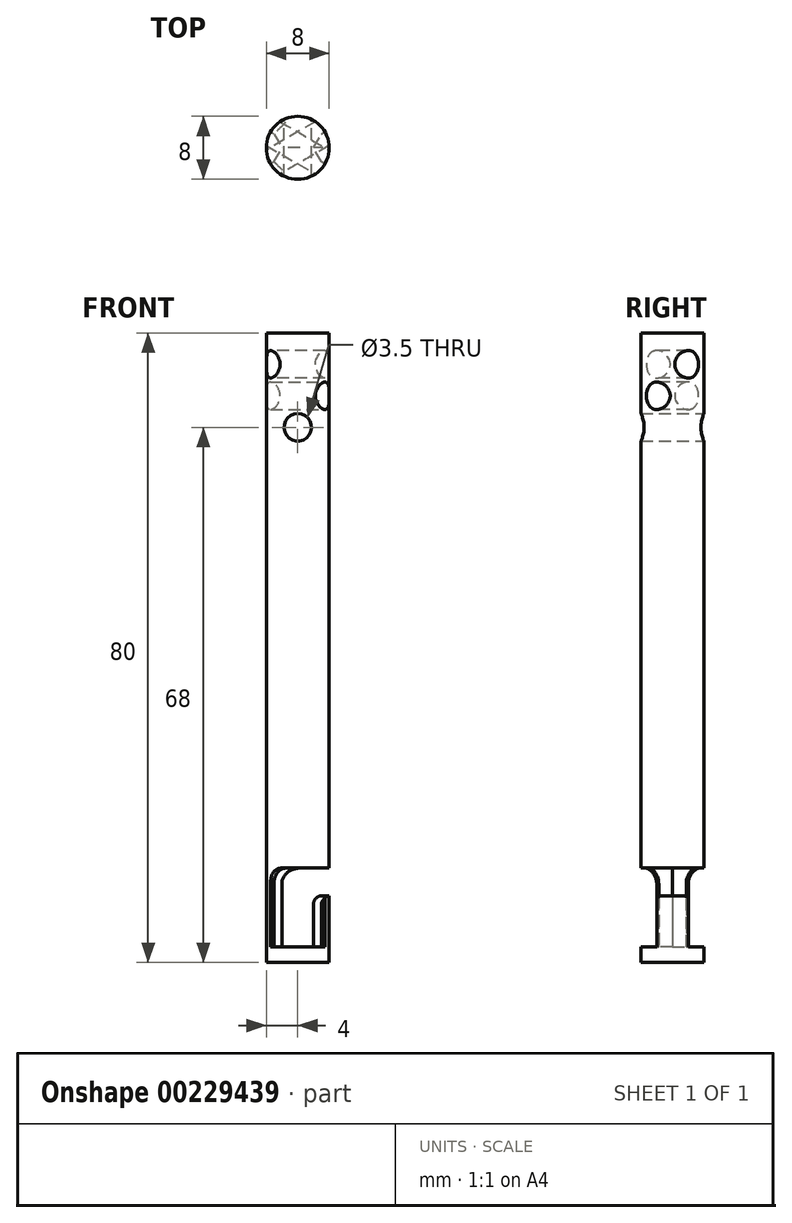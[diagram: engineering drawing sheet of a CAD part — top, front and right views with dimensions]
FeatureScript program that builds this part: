
annotation { "Feature Type Name" : "Feature", "Feature Type Description" : "" }
export const myFeature = defineFeature(function(context is Context, id is Id, definition is map)
    precondition{}
    {
        {
            var Q0;
            Q0=qCreatedBy(makeId("Top.planeOp"),FACE);
            cPlane(context, id + "F0", {"entities" : qUnion([Q0]), "cplaneType" : CPlaneType.OFFSET, "offset" : 1 * mm, "width" : 150 * mm, "height" : 150 * mm});
        }
        {
            var Q0;
            Q0=qCreatedBy(makeId("Front.planeOp"),FACE);
            var sketch = newSketch(context, id + "F1", { "sketchPlane" : qUnion([Q0])});
            skLineSegment(sketch, "E0", {"start": v(0, 0) * mm, "end": v(0, 56.56) * mm});
            skSolve(sketch);
        }
        {
            var Q0;
            Q0=sQuery(id+"F1.wireOp",EDGE,"E0");
            var Q1;
            Q1=qCreatedBy(makeId("Front.planeOp"),FACE);
            cPlane(context, id + "F2", {"entities" : qUnion([Q0, Q1]), "cplaneType" : CPlaneType.LINE_ANGLE, "offset" : 25 * mm, "angle" : 60 * degree, "width" : 150 * mm, "height" : 150 * mm});
        }
        {
            var Q0;
            Q0=sQuery(id+"F1.wireOp",EDGE,"E0");
            var Q1;
            Q1=qCreatedBy(makeId("Front.planeOp"),FACE);
            cPlane(context, id + "F3", {"entities" : qUnion([Q0, Q1]), "cplaneType" : CPlaneType.LINE_ANGLE, "offset" : 25 * mm, "angle" : 120 * degree, "width" : 150 * mm, "height" : 150 * mm});
        }
        {
            var Q0;
            Q0=qCreatedBy(makeId("Front.planeOp"),FACE);
            var sketch = newSketch(context, id + "F4", { "sketchPlane" : qUnion([Q0])});
            skCircle(sketch, "E1", {"center": v(0, 8) * mm, "radius": 1.75 * mm});
            skSolve(sketch);
        }
        {
            var Q0;
            Q0=qCreatedBy(id+"F2.planeOp",FACE);
            var sketch = newSketch(context, id + "F5", { "sketchPlane" : qUnion([Q0])});
            skCircle(sketch, "E2", {"center": v(0, 12) * mm, "radius": 1.75 * mm});
            skSolve(sketch);
        }
        {
            var Q0;
            Q0=qCreatedBy(id+"F3.planeOp",FACE);
            var sketch = newSketch(context, id + "F6", { "sketchPlane" : qUnion([Q0])});
            skCircle(sketch, "E3", {"center": v(0, 16) * mm, "radius": 1.75 * mm});
            skSolve(sketch);
        }
        {
            var Q0;
            Q0=qCreatedBy(id+"F0.planeOp",FACE);
            var sketch = newSketch(context, id + "F7", { "sketchPlane" : qUnion([Q0])});
            skCircle(sketch, "E4", {"center": v(0, 0) * mm, "radius": 4 * mm});
            skSolve(sketch);
        }
        {
            var Q0;
            Q0=makeQuery(id+"F7.imprint","IMPRINT",FACE,{"disambiguationData":[TD([[makeQuery(id+"F7.imprint","IMPRINT",EDGE,{"derivedFrom":sQuery(id+"F7.wireOp",EDGE,"E4")}),1.0]])]});
            extrude(context, id + "F8", {"entities" : qUnion([Q0]), "depth" : 19 * mm, "hasSecondDirection" : true, "secondDirectionOppositeDirection" : true, "secondDirectionDepth" : 61 * mm});
        }
        {
            var Q0;
            Q0 = qSketchRegion(id + "F6", true);
            extrude(context, id + "F9", {"entities" : qUnion([Q0]), "operationType" : NewBodyOperationType.REMOVE, "endBound" : BoundingType.UP_TO_NEXT, "oppositeDirection" : true, "depth" : 25 * mm, "hasSecondDirection" : true, "secondDirectionOppositeDirection" : false, "secondDirectionDepth" : 25 * mm});
        }
        {
            var Q0;
            Q0 = qSketchRegion(id + "F5", true);
            extrude(context, id + "F10", {"entities" : qUnion([Q0]), "operationType" : NewBodyOperationType.REMOVE, "endBound" : BoundingType.UP_TO_NEXT, "depth" : 25 * mm, "hasSecondDirection" : true, "secondDirectionBound" : SecondDirectionBoundingType.UP_TO_NEXT, "secondDirectionOppositeDirection" : true, "secondDirectionDepth" : 25 * mm});
        }
        {
            var Q0;
            Q0 = qSketchRegion(id + "F4", true);
            extrude(context, id + "F11", {"entities" : qUnion([Q0]), "operationType" : NewBodyOperationType.REMOVE, "endBound" : BoundingType.UP_TO_NEXT, "depth" : 25 * mm, "hasSecondDirection" : true, "secondDirectionBound" : SecondDirectionBoundingType.UP_TO_NEXT, "secondDirectionOppositeDirection" : true, "secondDirectionDepth" : 25 * mm});
        }
        {
            var Q0;
            Q0=qCreatedBy(makeId("Front.planeOp"),FACE);
            var sketch = newSketch(context, id + "F12", { "sketchPlane" : qUnion([Q0])});
            skLineSegment(sketch, "E5.bottom", {"start": v(-1.75, -58) * mm, "end": v(1.75, -58) * mm});
            skLineSegment(sketch, "E5.top", {"start": v(-1.75, -48) * mm, "end": v(1.75, -48) * mm});
            skLineSegment(sketch, "E5.left", {"start": v(-1.75, -58) * mm, "end": v(-1.75, -48) * mm});
            skLineSegment(sketch, "E5.right", {"start": v(1.75, -58) * mm, "end": v(1.75, -48) * mm});
            skLineSegment(sketch, "E6.bottom", {"start": v(-1.75, -48) * mm, "end": v(6.64, -48) * mm});
            skLineSegment(sketch, "E6.top", {"start": v(-1.75, -51.5) * mm, "end": v(6.64, -51.5) * mm});
            skLineSegment(sketch, "E6.left", {"start": v(-1.75, -48) * mm, "end": v(-1.75, -51.5) * mm});
            skLineSegment(sketch, "E6.right", {"start": v(6.64, -48) * mm, "end": v(6.64, -51.5) * mm});
            skSolve(sketch);
        }
        {
            var Q0;
            Q0=qCreatedBy(makeId("Right.planeOp"),FACE);
            var sketch = newSketch(context, id + "F13", { "sketchPlane" : qUnion([Q0])});
            skLineSegment(sketch, "E7.bottom", {"start": v(-7, -58) * mm, "end": v(-1, -58) * mm});
            skLineSegment(sketch, "E7.top", {"start": v(-7, -48) * mm, "end": v(-1, -48) * mm});
            skLineSegment(sketch, "E7.left", {"start": v(-7, -58) * mm, "end": v(-7, -48) * mm});
            skLineSegment(sketch, "E7.right", {"start": v(-1, -58) * mm, "end": v(-1, -48) * mm});
            skSolve(sketch);
        }
        {
            var Q0;
            Q0=makeQuery(id+"F13.imprint","IMPRINT",FACE,{"disambiguationData":[TD([[makeQuery(id+"F13.imprint","IMPRINT",EDGE,{"derivedFrom":sQuery(id+"F13.wireOp",EDGE,"E7.bottom")}),1.0]])]});
            var Q1;
            Q1=sQuery(id+"F13.wireOp",EDGE,"E7.left");
            var Q2;
            Q2=sQuery(id+"F1.wireOp",EDGE,"E0");
            revolve(context, id + "F14", {"operationType" : NewBodyOperationType.REMOVE, "surfaceOperationType" : NewSurfaceOperationType.NEW, "entities" : qUnion([Q0]), "surfaceEntities" : qUnion([Q1]), "axis" : qUnion([Q2]), "revolveType" : RevolveType.SYMMETRIC, "oppositeDirection" : true, "angle" : 120 * degree});
        }
        {
            var Q0;
            Q0=qCreatedBy(makeId("Right.planeOp"),FACE);
            var sketch = newSketch(context, id + "F15", { "sketchPlane" : qUnion([Q0])});
            skLineSegment(sketch, "E8.bottom", {"start": v(1, -58) * mm, "end": v(7, -58) * mm});
            skLineSegment(sketch, "E8.top", {"start": v(1, -48) * mm, "end": v(7, -48) * mm});
            skLineSegment(sketch, "E8.left", {"start": v(1, -58) * mm, "end": v(1, -48) * mm});
            skLineSegment(sketch, "E8.right", {"start": v(7, -58) * mm, "end": v(7, -48) * mm});
            skSolve(sketch);
        }
        {
            var Q0;
            Q0 = qSketchRegion(id + "F15", true);
            var Q1;
            Q1=sQuery(id+"F1.wireOp",EDGE,"E0");
            revolve(context, id + "F16", {"operationType" : NewBodyOperationType.REMOVE, "surfaceOperationType" : NewSurfaceOperationType.NEW, "entities" : qUnion([Q0]), "axis" : qUnion([Q1]), "revolveType" : RevolveType.SYMMETRIC, "angle" : 120 * degree});
        }
        {
            var Q0;
            Q0 = qSketchRegion(id + "F12", true);
            var Q1;
            Q1=sQuery(id+"F12.wireOp",EDGE,"SAmgIPEb-TWhO-SjVr-rJ2Y-Q6ch8T96Yinj");
            var Q2;
            Q2=sQuery(id+"F12.wireOp",EDGE,"V83VEsyv-MSzQ-oQPX-2e80-Iq0brfELiZnj.bottom");
            var Q3;
            Q3=sQuery(id+"F12.wireOp",EDGE,"V83VEsyv-MSzQ-oQPX-2e80-Iq0brfELiZnj.right");
            var Q4;
            Q4=sQuery(id+"F12.wireOp",EDGE,"V83VEsyv-MSzQ-oQPX-2e80-Iq0brfELiZnj.top");
            var Q5;
            Q5=sQuery(id+"F12.wireOp",EDGE,"7jSH2nb5-ehXd-Dpum-2Iuk-bTiolaQdSqVP.left");
            var Q6;
            Q6=sQuery(id+"F12.wireOp",EDGE,"7jSH2nb5-ehXd-Dpum-2Iuk-bTiolaQdSqVP.right");
            var Q7;
            Q7=sQuery(id+"F12.wireOp",EDGE,"cEcL3S88-yEdN-HCXQ-9xUG-hMFvsOIPaXgE");
            extrude(context, id + "F17", {"entities" : qUnion([Q0]), "operationType" : NewBodyOperationType.REMOVE, "surfaceEntities" : qUnion([Q1, Q2, Q3, Q4, Q5, Q6, Q7]), "oppositeDirection" : true, "depth" : 25 * mm, "hasSecondDirection" : true, "secondDirectionOppositeDirection" : false, "secondDirectionDepth" : 25 * mm});
        }
        {
            var Q0;
            Q0=qCreatedBy(makeId("Front.planeOp"),FACE);
            var Q1;
            Q1=sQuery(id+"F1.wireOp",EDGE,"E0");
            cPlane(context, id + "F18", {"entities" : qUnion([Q0, Q1]), "cplaneType" : CPlaneType.LINE_ANGLE, "offset" : 25 * mm, "angle" : 30 * degree, "width" : 150 * mm, "height" : 150 * mm});
        }
        {
            var Q0;
            Q0=qCreatedBy(makeId("Front.planeOp"),FACE);
            var Q1;
            Q1=sQuery(id+"F1.wireOp",EDGE,"E0");
            cPlane(context, id + "F19", {"entities" : qUnion([Q0, Q1]), "cplaneType" : CPlaneType.LINE_ANGLE, "offset" : 25 * mm, "angle" : -30 * degree, "width" : 150 * mm, "height" : 150 * mm});
        }
        {
            var Q0;
            Q0=qCreatedBy(id+"F18.planeOp",FACE);
            var sketch = newSketch(context, id + "F20", { "sketchPlane" : qUnion([Q0])});
            skLineSegment(sketch, "E9.bottom", {"start": v(1.75, -48) * mm, "end": v(-1.75, -48) * mm});
            skLineSegment(sketch, "E9.top", {"start": v(1.75, -58) * mm, "end": v(-1.75, -58) * mm});
            skLineSegment(sketch, "E9.left", {"start": v(1.75, -48) * mm, "end": v(1.75, -58) * mm});
            skLineSegment(sketch, "E9.right", {"start": v(-1.75, -48) * mm, "end": v(-1.75, -58) * mm});
            skSolve(sketch);
        }
        {
            var Q0;
            Q0=qCreatedBy(id+"F19.planeOp",FACE);
            var sketch = newSketch(context, id + "F21", { "sketchPlane" : qUnion([Q0])});
            skLineSegment(sketch, "E10.bottom", {"start": v(-1.75, -58) * mm, "end": v(1.75, -58) * mm});
            skLineSegment(sketch, "E10.top", {"start": v(-1.75, -48) * mm, "end": v(1.75, -48) * mm});
            skLineSegment(sketch, "E10.left", {"start": v(-1.75, -58) * mm, "end": v(-1.75, -48) * mm});
            skLineSegment(sketch, "E10.right", {"start": v(1.75, -58) * mm, "end": v(1.75, -48) * mm});
            skSolve(sketch);
        }
        {
            var Q0;
            Q0 = qSketchRegion(id + "F20", true);
            var Q1;
            Q1 = qSketchRegion(id + "F21", true);
            extrude(context, id + "F22", {"entities" : qUnion([Q0, Q1]), "operationType" : NewBodyOperationType.REMOVE, "endBound" : BoundingType.THROUGH_ALL, "depth" : 25 * mm, "offsetDistance" : 25 * mm, "hasSecondDirection" : true, "secondDirectionBound" : SecondDirectionBoundingType.THROUGH_ALL, "secondDirectionOppositeDirection" : true, "secondDirectionDepth" : 25 * mm});
        }
        {
            var Q0;
            Q0 = qSketchRegion(id + "F21", true);
            extrude(context, id + "F23", {"entities" : qUnion([Q0]), "operationType" : NewBodyOperationType.REMOVE, "endBound" : BoundingType.THROUGH_ALL, "oppositeDirection" : true, "depth" : 25 * mm, "offsetDistance" : 25 * mm, "hasSecondDirection" : true, "secondDirectionBound" : SecondDirectionBoundingType.THROUGH_ALL, "secondDirectionOppositeDirection" : false, "secondDirectionDepth" : 25 * mm});
        }
        {
            var Q0;
            Q0=makeQuery(id+"F22.boolean.opBoolean","INTERSECT",EDGE,{"derivedFrom":[makeQuery(id+"F17.boolean.opBoolean","COPY",FACE,{"derivedFrom":makeQuery(id+"F17.opExtrude","SWEPT_FACE",FACE,{"disambiguationData":[OSD([sQuery(id+"F12.wireOp",EDGE,"E6.top")])]})}),makeQuery(id+"F22.opExtrude","SWEPT_FACE",FACE,{"disambiguationData":[OSD([sQuery(id+"F20.wireOp",EDGE,"E9.right")])]})]});
            var Q1;
            Q1=makeQuery(id+"F23.boolean.opBoolean","INTERSECT",EDGE,{"derivedFrom":[makeQuery(id+"F17.boolean.opBoolean","COPY",FACE,{"derivedFrom":makeQuery(id+"F17.opExtrude","SWEPT_FACE",FACE,{"disambiguationData":[OSD([sQuery(id+"F12.wireOp",EDGE,"E6.top")])]})}),makeQuery(id+"F23.opExtrude","SWEPT_FACE",FACE,{"disambiguationData":[OSD([sQuery(id+"F21.wireOp",EDGE,"E10.left")])]})]});
            fillet(context, id + "F24", {"entities" : qUnion([Q0, Q1]), "radius" : 1 * mm, "tangentPropagation" : true, "defaultsChanged" : true, "vertexSettings" : [], "allowEdgeOverflow" : false});
        }
        {
            var Q0;
            Q0=makeQuery(id+"F22.boolean.opBoolean","COPY",EDGE,{"derivedFrom":makeQuery(id+"F22.opExtrude","SWEPT_EDGE",EDGE,{"disambiguationData":[OSD([sQuery(id+"F20.wireOp",EDGE,"E9.bottom"),sQuery(id+"F20.wireOp",EDGE,"E9.left")])]})});
            var Q1;
            Q1=makeQuery(id+"F23.boolean.opBoolean","COPY",EDGE,{"derivedFrom":makeQuery(id+"F23.opExtrude","SWEPT_EDGE",EDGE,{"disambiguationData":[OSD([sQuery(id+"F21.wireOp",EDGE,"E10.top"),sQuery(id+"F21.wireOp",EDGE,"E10.right")])]})});
            var Q2;
            Q2=makeQuery(id+"F14.boolean.opBoolean","COPY",EDGE,{"derivedFrom":makeQuery(id+"F14.opRevolve","CAP_EDGE",EDGE,{"disambiguationData":[OSD([sQuery(id+"F13.wireOp",EDGE,"E7.top")])],"isStart":false})});
            var Q3;
            Q3=makeQuery(id+"F16.boolean.opBoolean","COPY",EDGE,{"derivedFrom":makeQuery(id+"F16.opRevolve","CAP_EDGE",EDGE,{"disambiguationData":[OSD([sQuery(id+"F15.wireOp",EDGE,"E8.top")])],"isStart":false})});
            fillet(context, id + "F25", {"entities" : qUnion([Q0, Q1, Q2, Q3]), "radius" : 2 * mm, "tangentPropagation" : true, "defaultsChanged" : true, "vertexSettings" : [], "allowEdgeOverflow" : false});
        }
    });
